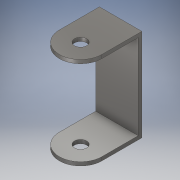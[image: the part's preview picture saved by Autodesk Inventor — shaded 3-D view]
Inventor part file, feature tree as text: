
AUTODESK INVENTOR PART (.ipt)
format: ipt  version: 2019 (Build 230136000, 136)  size: 134,144 bytes
history: native  units: mm
features: extrude x3, sketch x3, projected_geometry x2
ambient origin geometry x8: Origin, YZ Plane, XZ Plane, XY Plane, X Axis, Y Axis, Z Axis, Center Point
bodies: Solid1 (feature_tree)
feature tree (8):
  extrude  "Extrusion1"  Depth=35.0mm
  extrude  "Extrusion2"  Depth=10.1mm
  extrude  "Extrusion3"  Depth=3.0mm
  sketch  "Sketch1"  dims[d0=35.0mm d1=33.0mm]
  sketch  "Sketch2"  dims[d2=90.0deg d3=10.1mm]
  projected_geometry  "Projected Loop1"
  sketch  "Sketch3"  dims[d4=3.0mm d5=0.0mm d6=3.0mm d7=70.0mm d8=0.0mm d9=3.0mm d10=0.0mm]
  projected_geometry  "Projected Loop2"
